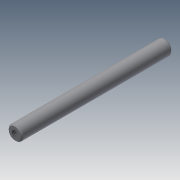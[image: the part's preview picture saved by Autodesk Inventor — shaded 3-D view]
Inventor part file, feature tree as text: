
AUTODESK INVENTOR PART (.ipt)
format: ipt  version: 2013 (Build 170138000, 138)  size: 80,896 bytes
history: native  units: mm
features: sketch x3, hole x2, extrude x1, chamfer x1
ambient origin geometry x8: Origin, YZ Plane, XZ Plane, XY Plane, X Axis, Y Axis, Z Axis, Center Point
bodies: Solid1 (feature_tree)
feature tree (7):
  extrude  "Extrusion1"  Depth=62.7mm TaperAngle=0.0deg
  hole  "Hole1"  [1 undecoded]
  hole  "Hole2"  [1 undecoded]
  chamfer  "Chamfer1"  [1 undecoded]
  sketch  "Sketch1"  dims[d0=6.0mm d1=62.7mm d2=0.0mm]
  sketch  "Sketch2"  dims[d3=2.459mm d4=6.0mm d5=4.0mm d6=2.0mm d7=90.0deg d8=8.0mm d9=0.0mm]
  sketch  "Sketch3"  dims[d10=2.459mm d11=6.0mm d12=4.0mm d13=2.0mm d14=90.0deg d15=8.0mm d16=0.0mm d17=0.5mm d18=2.0mm d19=45.0deg]
note: 3 required parameter values undecoded (feature->parameter linkage not recoverable at this tier; creation-order binding heuristic only, values carry confidence <= 0.55)
